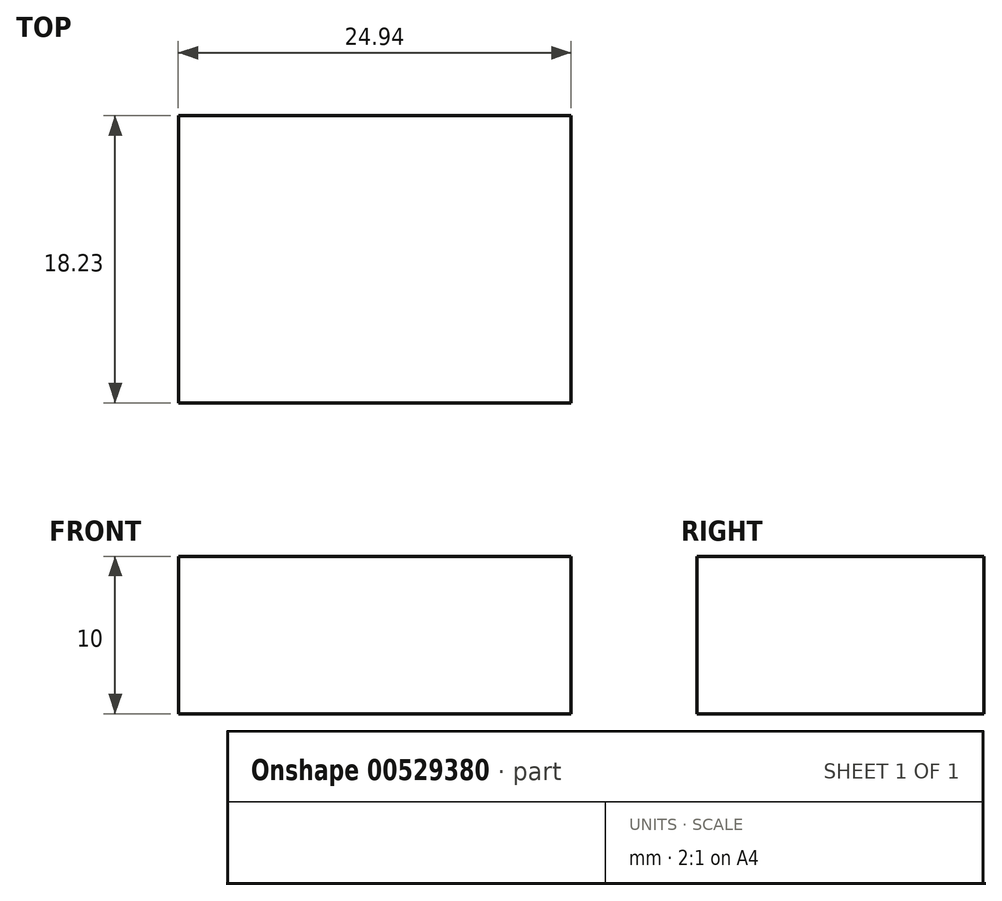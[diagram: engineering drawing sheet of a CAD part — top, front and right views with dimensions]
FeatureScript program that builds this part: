
annotation { "Feature Type Name" : "Feature", "Feature Type Description" : "" }
export const myFeature = defineFeature(function(context is Context, id is Id, definition is map)
    precondition{}
    {
        {
            var Q0;
            Q0=qCreatedBy(makeId("Top.planeOp"),FACE);
            var sketch = newSketch(context, id + "F0", { "sketchPlane" : qUnion([Q0])});
            skLineSegment(sketch, "E0.bottom", {"start": v(21.66, 35.5) * mm, "end": v(-21.66, 35.5) * mm});
            skLineSegment(sketch, "E0.top", {"start": v(21.66, 69.23) * mm, "end": v(-21.66, 69.23) * mm});
            skLineSegment(sketch, "E0.left", {"start": v(21.66, 35.5) * mm, "end": v(21.66, 69.23) * mm});
            skLineSegment(sketch, "E0.right", {"start": v(-21.66, 35.5) * mm, "end": v(-21.66, 69.23) * mm});
            skPoint(sketch, "E0.middle", {"position": v(0, 52.37) * mm});
            skLineSegment(sketch, "E1.bottom", {"start": v(55.8, -43.96) * mm, "end": v(2.15, -43.96) * mm});
            skLineSegment(sketch, "E1.top", {"start": v(55.8, 7.47) * mm, "end": v(2.15, 7.47) * mm});
            skLineSegment(sketch, "E1.left", {"start": v(55.8, -43.96) * mm, "end": v(55.8, 7.47) * mm});
            skLineSegment(sketch, "E1.right", {"start": v(2.15, -43.96) * mm, "end": v(2.15, 7.47) * mm});
            skPoint(sketch, "E1.middle", {"position": v(28.98, -18.24) * mm});
            skLineSegment(sketch, "E2.bottom", {"start": v(-32.32, -34.47) * mm, "end": v(-65.14, -34.47) * mm});
            skLineSegment(sketch, "E2.top", {"start": v(-32.32, -26.59) * mm, "end": v(-65.14, -26.59) * mm});
            skLineSegment(sketch, "E2.left", {"start": v(-32.32, -34.47) * mm, "end": v(-32.32, -26.59) * mm});
            skLineSegment(sketch, "E2.right", {"start": v(-65.14, -34.47) * mm, "end": v(-65.14, -26.59) * mm});
            skPoint(sketch, "E2.middle", {"position": v(-48.73, -30.53) * mm});
            skLineSegment(sketch, "E3.bottom", {"start": v(72.21, -100.6) * mm, "end": v(-163.94, -100.6) * mm});
            skLineSegment(sketch, "E3.top", {"start": v(72.21, 185.62) * mm, "end": v(-163.94, 185.62) * mm});
            skLineSegment(sketch, "E3.left", {"start": v(72.21, -100.6) * mm, "end": v(72.21, 185.62) * mm});
            skLineSegment(sketch, "E3.right", {"start": v(-163.94, -100.6) * mm, "end": v(-163.94, 185.62) * mm});
            skPoint(sketch, "E3.middle", {"position": v(-45.86, 42.51) * mm});
            skLineSegment(sketch, "E4.bottom", {"start": v(46.73, -16.62) * mm, "end": v(20.24, -16.62) * mm});
            skLineSegment(sketch, "E4.top", {"start": v(46.73, 418.44) * mm, "end": v(20.24, 418.44) * mm});
            skLineSegment(sketch, "E4.left", {"start": v(46.73, -16.62) * mm, "end": v(46.73, 418.44) * mm});
            skLineSegment(sketch, "E4.right", {"start": v(20.24, -16.62) * mm, "end": v(20.24, 418.44) * mm});
            skPoint(sketch, "E4.middle", {"position": v(33.48, 200.91) * mm});
            skLineSegment(sketch, "E5.bottom", {"start": v(145.77, 30.5) * mm, "end": v(120.83, 30.5) * mm});
            skLineSegment(sketch, "E5.top", {"start": v(145.77, 12.27) * mm, "end": v(120.83, 12.27) * mm});
            skLineSegment(sketch, "E5.left", {"start": v(145.77, 30.5) * mm, "end": v(145.77, 12.27) * mm});
            skLineSegment(sketch, "E5.right", {"start": v(120.83, 30.5) * mm, "end": v(120.83, 12.27) * mm});
            skPoint(sketch, "E5.middle", {"position": v(133.3, 21.39) * mm});
            skLineSegment(sketch, "E6.bottom", {"start": v(-25.45, -133.5) * mm, "end": v(246.16, -133.5) * mm});
            skLineSegment(sketch, "E6.top", {"start": v(-25.45, 426.7) * mm, "end": v(246.16, 426.7) * mm});
            skLineSegment(sketch, "E6.left", {"start": v(-25.45, -133.5) * mm, "end": v(-25.45, 426.7) * mm});
            skLineSegment(sketch, "E6.right", {"start": v(246.16, -133.5) * mm, "end": v(246.16, 426.7) * mm});
            skPoint(sketch, "E6.middle", {"position": v(110.36, 146.6) * mm});
            skSolve(sketch);
        }
        {
            var Q0;
            Q0=makeQuery(id+"F0.imprint","IMPRINT",FACE,{"disambiguationData":[TD([[makeQuery(id+"F0.imprint","IMPRINT",EDGE,{"derivedFrom":sQuery(id+"F0.wireOp",EDGE,"E5.bottom")}),1.0]])]});
            extrude(context, id + "F1", {"entities" : qUnion([Q0]), "depth" : 10 * mm, "offsetDistance" : 25.4 * mm});
        }
        {
            var Q0;
            Q0=qCreatedBy(makeId("Top.planeOp"),FACE);
            var sketch = newSketch(context, id + "F2", { "sketchPlane" : qUnion([Q0])});
            skArc(sketch, "E7", {"start": v(0, 183.27) * mm, "mid": v(-57.38, 135.62) * mm, "end": v(16.8, 127.74) * mm});
            skArc(sketch, "E8", {"start": v(-27.9, 220.9) * mm, "mid": v(-85.27, 231.29) * mm, "end": v(-69.71, 175.09) * mm});
            skArc(sketch, "E9", {"start": v(-69.71, 175.09) * mm, "mid": v(37.25, 372.37) * mm, "end": v(-83.98, 183.52) * mm});
            skArc(sketch, "E10", {"start": v(-128.7, 136.6) * mm, "mid": v(-94.52, 28.3) * mm, "end": v(-57.38, 135.62) * mm});
            skSolve(sketch);
        }
        {
            var Q0;
            Q0=sQuery(id+"F2.wireOp",EDGE,"E10");
            extrude(context, id + "F3", {"bodyType" : ToolBodyType.SURFACE, "surfaceEntities" : qUnion([Q0]), "depth" : 25.4 * mm, "offsetDistance" : 25.4 * mm});
        }
    });
